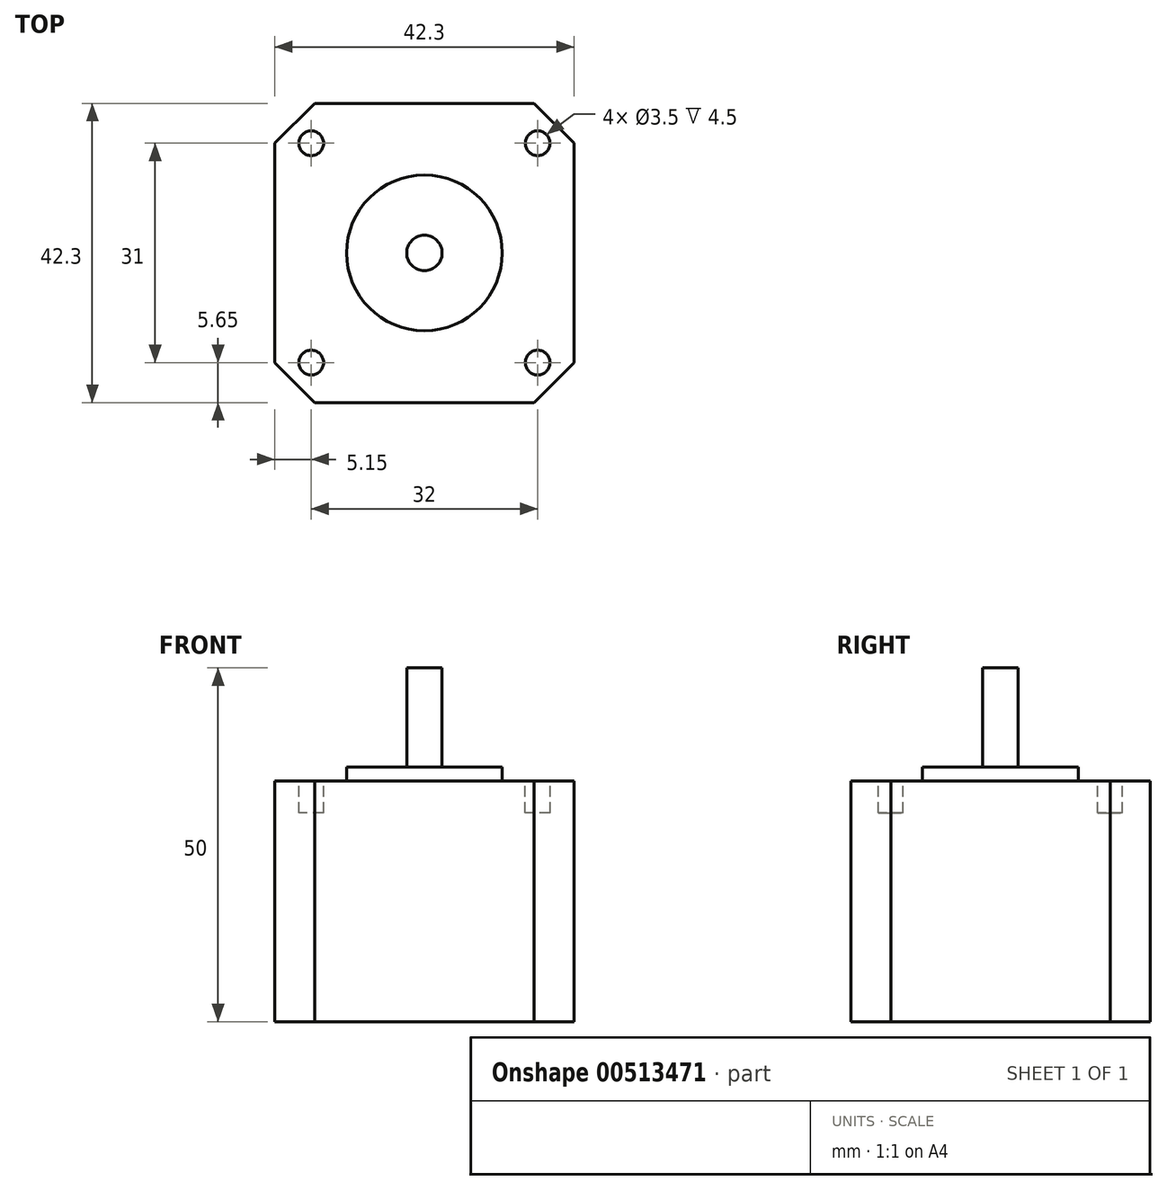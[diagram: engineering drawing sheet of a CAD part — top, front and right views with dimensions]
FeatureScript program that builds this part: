
annotation { "Feature Type Name" : "Feature", "Feature Type Description" : "" }
export const myFeature = defineFeature(function(context is Context, id is Id, definition is map)
    precondition{}
    {
        {
            var Q0;
            Q0=qCreatedBy(makeId("Top.planeOp"),FACE);
            var sketch = newSketch(context, id + "F0", { "sketchPlane" : qUnion([Q0])});
            skLineSegment(sketch, "E0.bottom", {"start": v(21.15, 21.15) * mm, "end": v(-21.15, 21.15) * mm});
            skLineSegment(sketch, "E0.top", {"start": v(21.15, -21.15) * mm, "end": v(-21.15, -21.15) * mm});
            skLineSegment(sketch, "E0.left", {"start": v(21.15, 21.15) * mm, "end": v(21.15, -21.15) * mm});
            skLineSegment(sketch, "E0.right", {"start": v(-21.15, 21.15) * mm, "end": v(-21.15, -21.15) * mm});
            skPoint(sketch, "E0.middle", {"position": v(0, 0) * mm});
            skSolve(sketch);
        }
        {
            var Q0;
            Q0=makeQuery(id+"F0.imprint","IMPRINT",FACE,{"disambiguationData":[TD([[makeQuery(id+"F0.imprint","IMPRINT",EDGE,{"derivedFrom":sQuery(id+"F0.wireOp",EDGE,"E0.bottom")}),1.0]])]});
            extrude(context, id + "F1", {"entities" : qUnion([Q0]), "depth" : 34 * mm});
        }
        {
            var Q0;
            Q0=makeQuery(id+"F1.opExtrude","CAP_FACE",FACE,{"disambiguationData":[OSD([sQuery(id+"F0.wireOp",EDGE,"E0.bottom"),sQuery(id+"F0.wireOp",EDGE,"E0.top"),sQuery(id+"F0.wireOp",EDGE,"E0.left"),sQuery(id+"F0.wireOp",EDGE,"E0.right")])],"isStart":false});
            var sketch = newSketch(context, id + "F2", { "sketchPlane" : qUnion([Q0])});
            skCircle(sketch, "E1", {"center": v(0, 0) * mm, "radius": 11 * mm});
            skSolve(sketch);
        }
        {
            var Q0;
            Q0=makeQuery(id+"F2.imprint","IMPRINT",FACE,{"disambiguationData":[TD([[makeQuery(id+"F2.imprint","IMPRINT",EDGE,{"derivedFrom":sQuery(id+"F2.wireOp",EDGE,"E1")}),1.0]])]});
            extrude(context, id + "F3", {"entities" : qUnion([Q0]), "operationType" : NewBodyOperationType.ADD, "depth" : 2 * mm});
        }
        {
            var Q0;
            Q0=makeQuery(id+"F3.opExtrude","CAP_FACE",FACE,{"disambiguationData":[OSD([sQuery(id+"F2.wireOp",EDGE,"E1")])],"isStart":false});
            var sketch = newSketch(context, id + "F4", { "sketchPlane" : qUnion([Q0])});
            skCircle(sketch, "E2", {"center": v(0, 0) * mm, "radius": 2.5 * mm});
            skSolve(sketch);
        }
        {
            var Q0;
            Q0=makeQuery(id+"F4.imprint","IMPRINT",FACE,{"disambiguationData":[TD([[makeQuery(id+"F4.imprint","IMPRINT",EDGE,{"derivedFrom":sQuery(id+"F4.wireOp",EDGE,"E2")}),1.0]])]});
            extrude(context, id + "F5", {"entities" : qUnion([Q0]), "operationType" : NewBodyOperationType.ADD, "depth" : (16 - 2) * mm});
        }
        {
            var Q0;
            Q0=makeQuery(id+"F1.opExtrude","SWEPT_EDGE",EDGE,{"disambiguationData":[OSD([sQuery(id+"F0.wireOp",EDGE,"E0.bottom"),sQuery(id+"F0.wireOp",EDGE,"E0.left")])]});
            var Q1;
            Q1=makeQuery(id+"F1.opExtrude","SWEPT_EDGE",EDGE,{"disambiguationData":[OSD([sQuery(id+"F0.wireOp",EDGE,"E0.bottom"),sQuery(id+"F0.wireOp",EDGE,"E0.right")])]});
            var Q2;
            Q2=makeQuery(id+"F1.opExtrude","SWEPT_EDGE",EDGE,{"disambiguationData":[OSD([sQuery(id+"F0.wireOp",EDGE,"E0.top"),sQuery(id+"F0.wireOp",EDGE,"E0.left")])]});
            var Q3;
            Q3=makeQuery(id+"F1.opExtrude","SWEPT_EDGE",EDGE,{"disambiguationData":[OSD([sQuery(id+"F0.wireOp",EDGE,"E0.top"),sQuery(id+"F0.wireOp",EDGE,"E0.right")])]});
            chamfer(context, id + "F6", {"entities" : qUnion([Q0, Q1, Q2, Q3]), "width" : (42.3 - 31) / 2 * mm, "tangentPropagation" : true});
        }
        {
            var Q0;
            Q0=makeQuery(id+"F1.opExtrude","CAP_FACE",FACE,{"disambiguationData":[OSD([sQuery(id+"F0.wireOp",EDGE,"E0.bottom"),sQuery(id+"F0.wireOp",EDGE,"E0.top"),sQuery(id+"F0.wireOp",EDGE,"E0.left"),sQuery(id+"F0.wireOp",EDGE,"E0.right")])],"isStart":false});
            var sketch = newSketch(context, id + "F7", { "sketchPlane" : qUnion([Q0])});
            skCircle(sketch, "E3", {"center": v(16, 15.5) * mm, "radius": 1.75 * mm});
            skCircle(sketch, "E4.MirrorC", {"center": v(-16, 15.5) * mm, "radius": 1.75 * mm});
            skCircle(sketch, "E5.MirrorC", {"center": v(16, -15.5) * mm, "radius": 1.75 * mm});
            skCircle(sketch, "E6.MirrorC", {"center": v(-16, -15.5) * mm, "radius": 1.75 * mm});
            skSolve(sketch);
        }
        {
            var Q0;
            Q0 = qSketchRegion(id + "F7", true);
            extrude(context, id + "F8", {"entities" : qUnion([Q0]), "operationType" : NewBodyOperationType.REMOVE, "oppositeDirection" : true, "depth" : 4.5 * mm});
        }
    });
